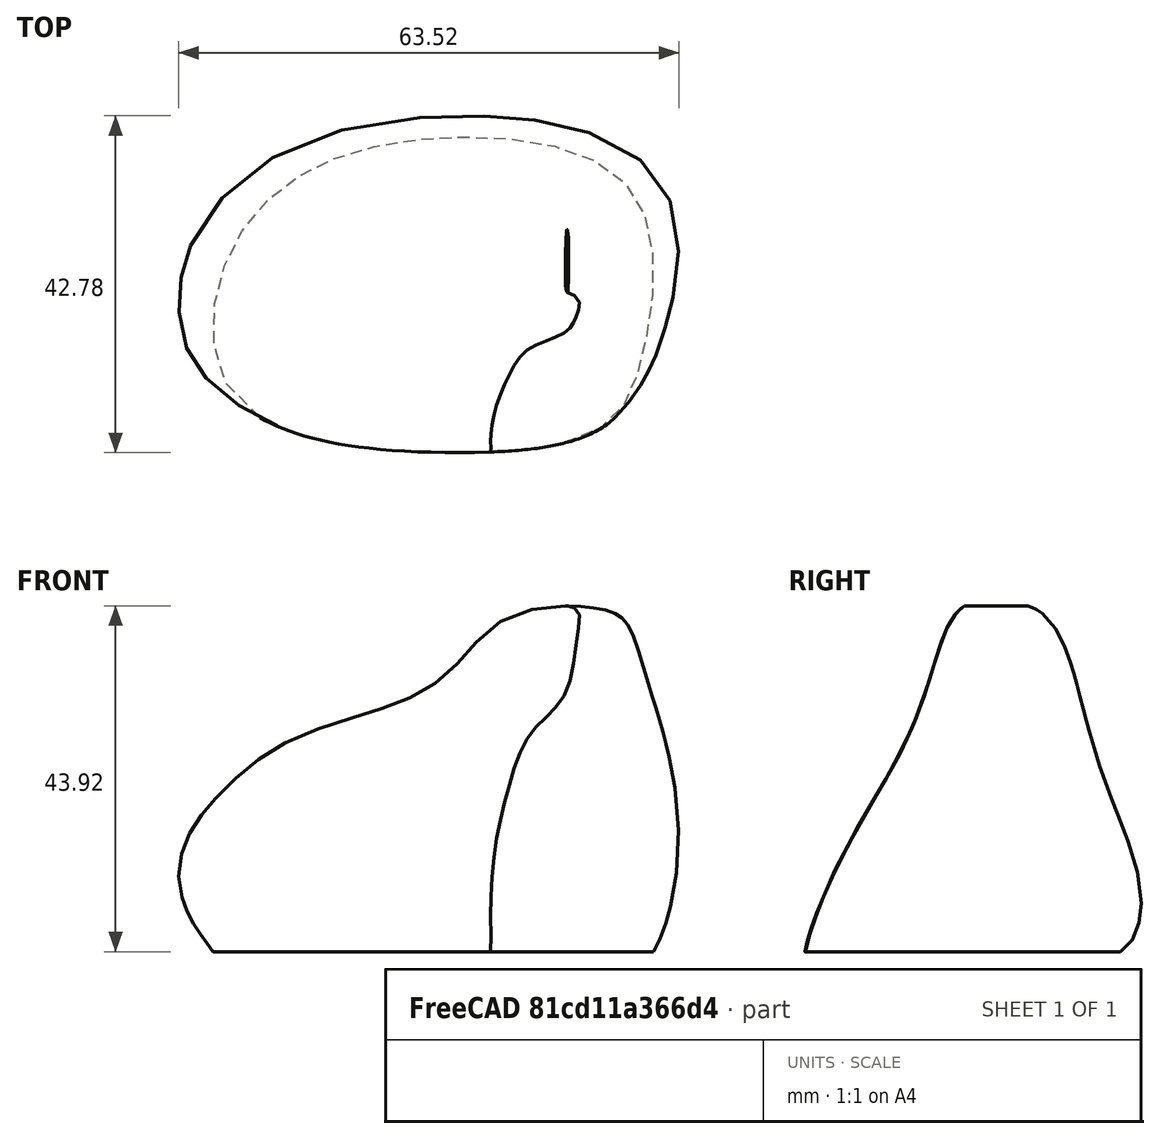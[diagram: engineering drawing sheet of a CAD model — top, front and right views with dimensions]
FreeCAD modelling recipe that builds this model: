
FCSTD DOCUMENT  (FreeCAD 1.0R39109 (Git))
Label: coral
License: All rights reserved
LicenseURL: https://en.wikipedia.org/wiki/All_rights_reserved
objects: Sketcher::SketchObject×3, PartDesign::Body×1, Part::FeaturePython×1, Part::Feature×1, Points::Feature×1, Points::Structured×1, Mesh::Feature×1
note: 9 computed .brp shape members not serialized (recipe doc carries the construction recipe); baked Part::Feature solids carry a one-line shape summary decoded from their .brp

FEATURE [Sketcher::SketchObject] Sketch
  ArcFitTolerance = 1e-06
  AttachmentSupport = -> [XY_Plane]
  FullyConstrained = false
  MakeInternals = false
  MapMode = 5
  sketch-geometry (17):
    g0-g8: Circle [constr] x9 (B-spline internal-alignment scaffolding for g9; pole/knot coordinates omitted)
    g9: BSplineCurve PolesCount=9 KnotsCount=7 Degree=3 IsPeriodic=0
    g10-g16: GeomPoint [constr] x7 (B-spline internal-alignment scaffolding for g9; pole/knot coordinates omitted)
  constraints (6):
    c: Weight(g0) = 1
    c: Equal(g0, g1-g8) x8
    c: InternalAlignment(g0-g8 -> g9) x9
    c: InternalAlignment(g10-g16 -> g9) x7
    c: PointOnObject(g0,g-2)
    c: Coincident(g8,g0)
FEATURE [Sketcher::SketchObject] Sketch001
  ArcFitTolerance = 1e-06
  AttachmentOffset = pos=(0,0,-23) rot=(0,0,1;0rad)
  AttachmentSupport = -> [XZ_Plane]
  FullyConstrained = false
  MakeInternals = false
  MapMode = 5
  Placement = pos=(0,23,-5.1e-15) rot=(1,0,0;1.5708rad)
  sketch-geometry (19):
    g0-g9: Circle [constr] x10 (B-spline internal-alignment scaffolding for g10; pole/knot coordinates omitted)
    g10: BSplineCurve PolesCount=10 KnotsCount=8 Degree=3 IsPeriodic=0
    g11-g18: GeomPoint [constr] x8 (B-spline internal-alignment scaffolding for g10; pole/knot coordinates omitted)
  constraints (7):
    c: Weight(g0) = 1
    c: Equal(g0, g1-g9) x9
    c: InternalAlignment(g0-g9 -> g10) x10
    c: InternalAlignment(g11-g18 -> g10) x8
    c: PointOnObject(g0,g-1)
    c: PointOnObject(g5,g-2)
    c: PointOnObject(g9,g-1)
FEATURE [Sketcher::SketchObject] Sketch002
  ArcFitTolerance = 1e-06
  AttachmentOffset = pos=(0,0,26) rot=(0,0,1;0rad)
  AttachmentSupport = -> [YZ_Plane]
  FullyConstrained = false
  MakeInternals = false
  MapMode = 5
  Placement = pos=(26,0,0) rot=(0.57735,0.57735,0.57735;2.0944rad)
  sketch-geometry (17):
    g0-g8: Circle [constr] x9 (B-spline internal-alignment scaffolding for g9; pole/knot coordinates omitted)
    g9: BSplineCurve PolesCount=9 KnotsCount=7 Degree=3 IsPeriodic=0
    g10-g16: GeomPoint [constr] x7 (B-spline internal-alignment scaffolding for g9; pole/knot coordinates omitted)
  constraints (9):
    c: Weight(g0) = 1
    c: Equal(g0,g1)
    c: Equal(g0,g2)
    c: Equal(g0,g3)
    c: Equal(g0, g5-g8) x4
    c: InternalAlignment(g0-g8 -> g9) x9
    c: InternalAlignment(g10-g16 -> g9) x7
    c: PointOnObject(g0,g-1)
    c: PointOnObject(g8,g-1)
FEATURE [PartDesign::Body] Body
  AllowCompound = false
  Group = -> [Sketch,Sketch001,Sketch002]
  Origin = -> Origin
FEATURE [Part::FeaturePython] CurvedArray  # WARN: FeaturePython — macro-defined, semantics opaque (R4)
  Axis = (0,0,1)
  Base = -> Sketch
  Distribution = 0
  DistributionReverse = false
  Hullcurves = -> [Sketch002,Sketch001]
  Items = 100
  KeepBase = 1
  LoftMaxDegree = 1
  MaxLoftSize = 100
  OffsetEnd = 0
  OffsetStart = 0
  Solid = false
  Surface = true
  Twist = 0
FEATURE [Part::Feature] CurvedArray_pts
  shape: bbox 63.5 x 42.79 x 43.92 mm, 0 faces, 0 solids (baked)
FEATURE [Points::Feature] Points
FEATURE [Points::Structured] Points__Structured_  label="Points (Structured)"
  Height = 6466
  Width = 6466
FEATURE [Mesh::Feature] Poisson
